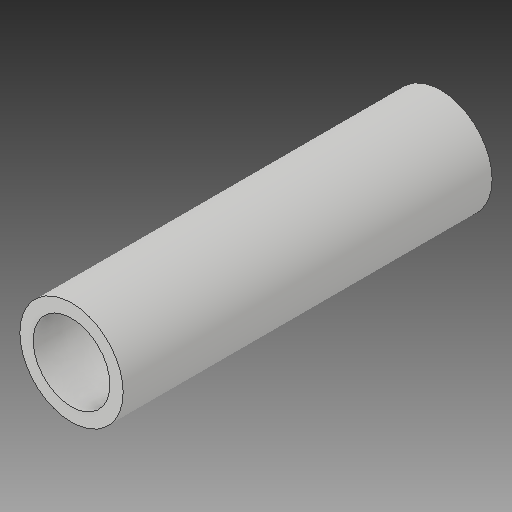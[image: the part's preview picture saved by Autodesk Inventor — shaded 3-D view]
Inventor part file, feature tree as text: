
AUTODESK INVENTOR PART (.ipt)
format: ipt  version: 2017 (Build 210142000, 142)  size: 98,304 bytes
history: native  units: mm
features: other x3, sketch x1
ambient origin geometry x8: Origin, YZ Plane, XZ Plane, XY Plane, X Axis, Y Axis, Z Axis, Center Point
bodies: Solid1 (feature_tree)
feature tree (4):
  other  "25mmspacer.ipt"
  other  "Solid1::25mmspacer.ipt"
  other  "TaggingFeature1"
  sketch  "Sketch1"  dims[d0=10.0mm]
